# Revit family: ledwaterproof-p3_l710-12_5w-4000_543022015500_b6a2
name_source: partatom
category: Leuchten
revit_build: Autodesk Revit 2016 (Build: 20190508_0715(x64)
units: mm (PartAtom-declared; Revit-internal decimal feet)

## family parameters
Basisbauteil = Fläche
Beim Laden mit Abzugskörper schneiden = Nein
Bemaßung runder Anschluss = Durchmesser verwenden
Gemeinsam genutzt = Nein
Lichtquelle = Nein
Raumberechnungspunkt = Nein
Teiletyp = Normal

## types (1)
- LEDWaterproof-P3 L710-12.5W-4000 (1 x LED, 1688 lm)
    Approval mark = CE, ENEC
    Beschreibung = Powerful range of waterproof luminaires in specific "sealed for life" design. Quick installation thanks to its screwless endcap. Supplied with vandal-proof stainless steel ceiling and suspension clips.
    CIE Flux Codes = 42 71 89 93 100
    Control Gear = Electronic ballast
    Height = 81 mm
    Hersteller = OPPLE
    Lamp Light Flux = 1688 lm
    Lamp count = 1
    Lampe = 1 x LED
    Length = 78 mm
    Luminous efficacy = 135 lm/W
    ModVariant = Nein
    Modell = 543022015500
    Mounting Place = Ceiling
    Mounting Type = Surface mounted
    Number of Poles = 1
    OnlyDefault = Ja
    Power Factor = 1
    Product Name = LEDWaterproof-P3 L710-12.5W-4000
    Product group = Waterproof Performer G3
    ProductGroupID = 348
    Protection Class = Protection class II
    Protection Degree = IP 65
    RLX_Detail_Level = 1
    RlxData = <blob elided: 145001 chars, md5=e6d4879a>
    Scheinlast = 13 VA
    Socket = socket
    Standby Power = 0 W
    System Light Flux = 1688 lm
    System Power = 13 W
    Typenbild = 543022015500.jpg
    Typenkommentare = Product without accessories
    URL = http://relux.com
    VarID = ---
    Voltage = 0 V
    Vorgabe-Ansicht = 1800 mm
    Weight = 0.00 kg
    Width = 710 mm

## geometry (parser evidence)
native form markers: Blend x4, Sweep x13
no freeform markers — native parametric forms only
